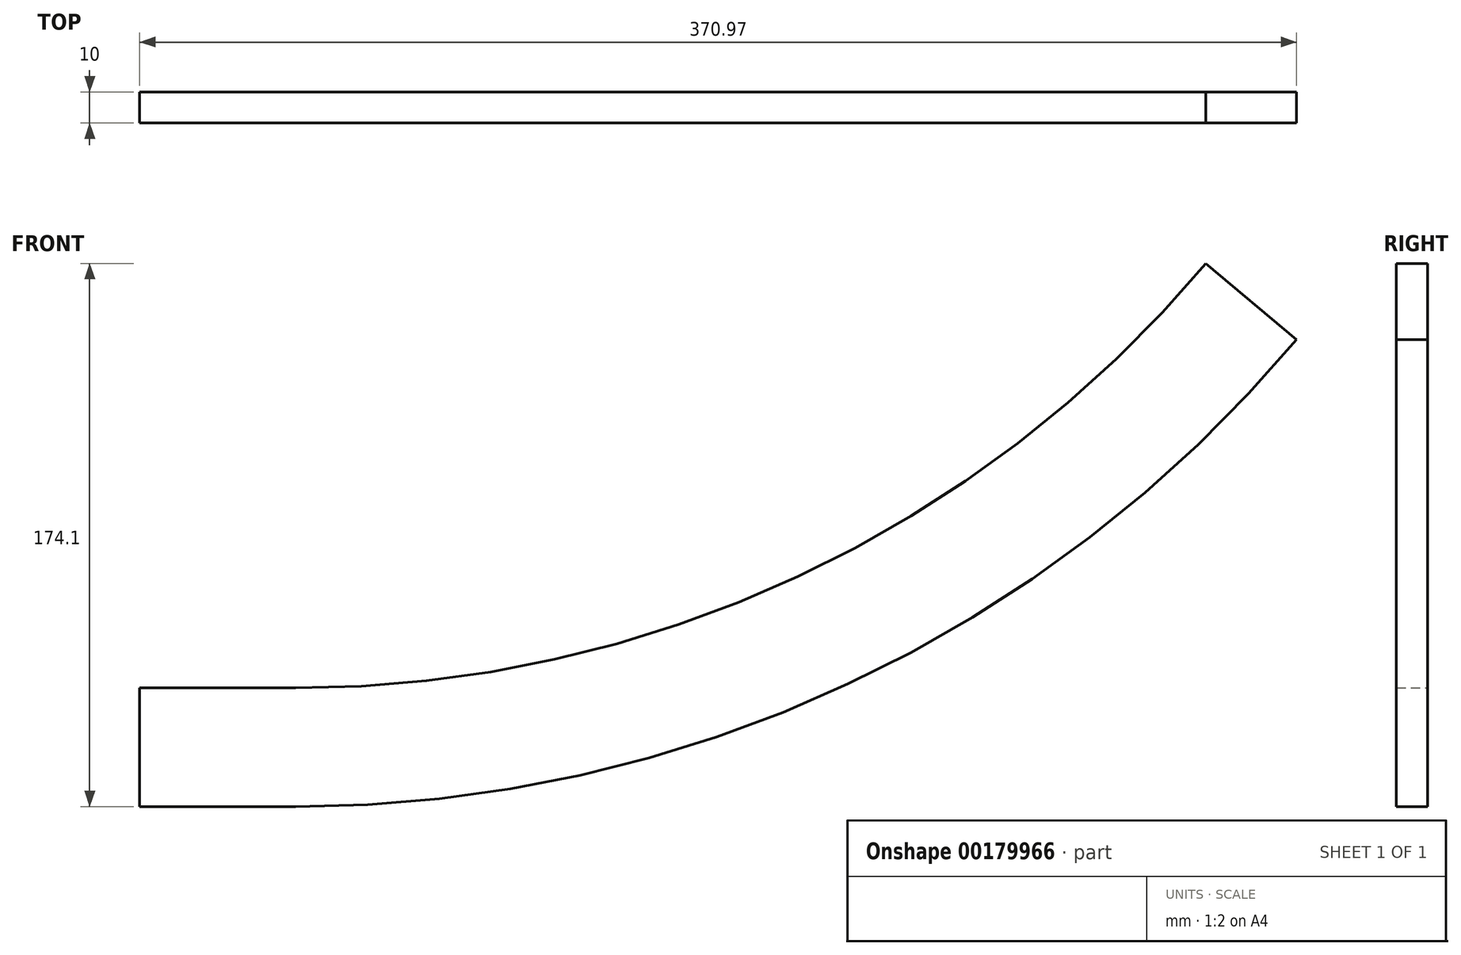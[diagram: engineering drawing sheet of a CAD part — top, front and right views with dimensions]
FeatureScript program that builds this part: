
annotation { "Feature Type Name" : "Feature", "Feature Type Description" : "" }
export const myFeature = defineFeature(function(context is Context, id is Id, definition is map)
    precondition{}
    {
        {
            var Q0;
            Q0=qCreatedBy(makeId("Front.planeOp"),FACE);
            var sketch = newSketch(context, id + "F0", { "sketchPlane" : qUnion([Q0])});
            skLineSegment(sketch, "E0.left", {"start": v(0, 0) * mm, "end": v(0, 400) * mm, "construction": true});
            skArc(sketch, "E1", {"start": v(0, 0) * mm, "mid": v(200, 53.59) * mm, "end": v(346.41, 200) * mm, "construction": true});
            skLineSegment(sketch, "E2", {"start": v(0, 400) * mm, "end": v(346.41, 200) * mm, "construction": true});
            skArc(sketch, "E3.0", {"start": v(0, -19) * mm, "mid": v(209.5, 37.14) * mm, "end": v(362.86, 190.5) * mm});
            skArc(sketch, "E4.0", {"start": v(0, 19) * mm, "mid": v(190.5, 70.04) * mm, "end": v(329.96, 209.5) * mm});
            skLineSegment(sketch, "E5", {"start": v(0, 400) * mm, "end": v(320.97, 130.67) * mm});
            skLineSegment(sketch, "E6", {"start": v(0, -19) * mm, "end": v(0, 19) * mm});
            skLineSegment(sketch, "E7", {"start": v(0, 19) * mm, "end": v(-50, 19) * mm});
            skLineSegment(sketch, "E8", {"start": v(-50, 19) * mm, "end": v(-50, -19) * mm});
            skLineSegment(sketch, "E9", {"start": v(-50, -19) * mm, "end": v(0, -19) * mm});
            skSolve(sketch);
        }
        {
            var Q0;
            Q0=qSketchRegion(id+"F0",true);
            extrude(context, id + "F1", {"entities" : qUnion([Q0]), "depth" : 10 * mm});
        }
    });
